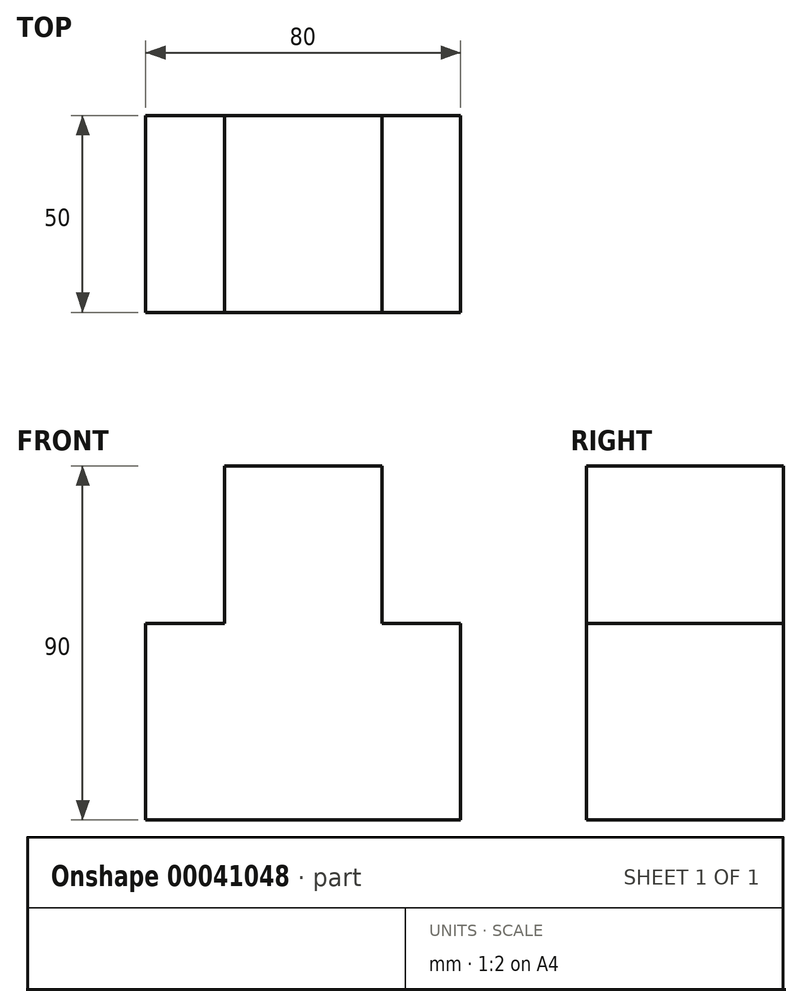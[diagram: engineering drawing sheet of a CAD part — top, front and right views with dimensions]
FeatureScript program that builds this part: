
annotation { "Feature Type Name" : "Feature", "Feature Type Description" : "" }
export const myFeature = defineFeature(function(context is Context, id is Id, definition is map)
    precondition{}
    {
        {
            var Q0;
            Q0=qCreatedBy(makeId("Front.planeOp"),FACE);
            var sketch = newSketch(context, id + "F0", { "sketchPlane" : qUnion([Q0])});
            skLineSegment(sketch, "E0", {"start": v(-43.91, 26.28) * mm, "end": v(-43.91, -23.72) * mm});
            skLineSegment(sketch, "E1", {"start": v(-43.91, -23.72) * mm, "end": v(36.09, -23.72) * mm});
            skLineSegment(sketch, "E2", {"start": v(36.09, -23.72) * mm, "end": v(36.09, 26.28) * mm});
            skLineSegment(sketch, "E3", {"start": v(36.09, 26.28) * mm, "end": v(16.09, 26.28) * mm});
            skLineSegment(sketch, "E4", {"start": v(16.09, 26.28) * mm, "end": v(16.09, 66.28) * mm});
            skLineSegment(sketch, "E5", {"start": v(16.09, 66.28) * mm, "end": v(-23.91, 66.28) * mm});
            skLineSegment(sketch, "E6", {"start": v(-23.91, 66.28) * mm, "end": v(-23.91, 26.28) * mm});
            skLineSegment(sketch, "E7", {"start": v(-23.91, 26.28) * mm, "end": v(-43.91, 26.28) * mm});
            skSolve(sketch);
        }
        {
            var Q0;
            Q0=makeQuery(id+"F0.imprint","IMPRINT",FACE,{"disambiguationData":[TD([[makeQuery(id+"F0.imprint","IMPRINT",EDGE,{"derivedFrom":sQuery(id+"F0.wireOp",EDGE,"E0")}),1.0]])]});
            extrude(context, id + "F1", {"entities" : qUnion([Q0]), "depth" : 50 * mm});
        }
    });
